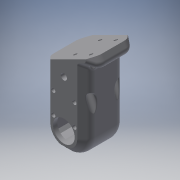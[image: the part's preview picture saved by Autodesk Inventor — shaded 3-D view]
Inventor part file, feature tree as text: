
AUTODESK INVENTOR PART (.ipt)
format: ipt  version: 2018 (Build 220112000, 112)  size: 1,027,072 bytes
history: native  units: mm
features: sketch x30, projected_geometry x26, extrude x23, hole x10, fillet x10, chamfer x3, mirror x1, plane x1
ambient origin geometry x8: Origin, YZ Plane, XZ Plane, XY Plane, X Axis, Y Axis, Z Axis, Center Point
bodies: Solid1 (feature_tree)
feature tree (104):
  extrude  "Extrusion1"  Depth=45.0mm
  extrude  "Extrusion2"  Depth=2.25mm
  hole  "Hole1"  [1 undecoded]
  hole  "Hole2"  [1 undecoded]
  fillet  "Fillet1"  Radius=14.0mm
  extrude  "Extrusion3"  Depth=18.5mm
  extrude  "Extrusion4"  Depth=10.0mm
  extrude  "Extrusion5"  Depth=2.0mm
  extrude  "Extrusion6"  Depth=2.0mm
  hole  "Hole3"  [1 undecoded]
  extrude  "Extrusion7"  Depth=0.5mm
  extrude  "Extrusion8"  Depth=5.0mm TaperAngle=0.0deg
  extrude  "Extrusion9"  Depth=10.0mm
  extrude  "Extrusion10"  Depth=10.0mm
  extrude  "Extrusion11"  Depth=14.5mm
  extrude  "Extrusion12"  Depth=20.0mm
  extrude  "Extrusion13"  Depth=5.0mm
  extrude  "Extrusion14"  Depth=2.25mm
  extrude  "Extrusion15"  Depth=5.0mm
  extrude  "Extrusion16"  Depth=9.0mm
  extrude  "Extrusion17"  Depth=1.0mm
  chamfer  "Chamfer1"  Distance=1.0mm
  fillet  "Fillet7"  Radius=20.7mm
  fillet  "Fillet8"  Radius=32.0mm
  mirror  "Mirror1"
  extrude  "Extrusion24"  Depth=1.0mm TaperAngle=0.0deg
  extrude  "Extrusion25"  Depth=8.0mm
  extrude  "Extrusion26"  Depth=0.2mm TaperAngle=0.0deg
  extrude  "Extrusion27"  Depth=0.5mm TaperAngle=0.0deg
  extrude  "Extrusion28"  Depth=5.0mm TaperAngle=0.0deg
  chamfer  "Chamfer5"  Distance=5.0mm
  fillet  "Fillet18"  Radius=0.2mm
  fillet  "Fillet19"  Radius=0.2mm
  extrude  "Extrusion29"  Depth=1.5mm
  chamfer  "Chamfer6"  Distance=40.0mm
  hole  "Hole10"  [1 undecoded]
  plane  "Work Plane2"
  hole  "Hole11"  [1 undecoded]
  fillet  "Fillet20"  Radius=10.0mm
  sketch  "Sketch43"  dims[d102=2.5mm d103=2.0mm d104=45.0deg d105=1.5mm]
  hole  "Hole12"  [1 undecoded]
  hole  "Hole13"  [1 undecoded]
  hole  "Hole14"  [1 undecoded]
  fillet  "Fillet21"  Radius=8.0mm
  fillet  "Fillet22"  Radius=10.0mm
  hole  "Hole15"  [1 undecoded]
  fillet  "Fillet23"  Radius=2.0mm
  hole  "Hole16"  [1 undecoded]
  fillet  "Fillet24"  Radius=8.0mm
  sketch  "Sketch1"  dims[d0=24.5mm d1=45.0mm]
  sketch  "Sketch2"  dims[d2=1.95mm d3=0.0mm d4=2.25mm]
  projected_geometry  "Projected Loop1"
  sketch  "Sketch3"  dims[d5=20.0mm d6=2.25mm]
  projected_geometry  "Projected Loop2"
  sketch  "Sketch4"  dims[d7=5.25mm d8=5.25mm d9=14.0mm]
  projected_geometry  "Projected Loop3"
  sketch  "Sketch5"  dims[d10=5.25mm d11=18.5mm]
  projected_geometry  "Projected Loop4"
  sketch  "Sketch6"  dims[d12=10.0mm d13=0.0mm d14=20.5mm]
  projected_geometry  "Projected Loop5"
  sketch  "Sketch7"  dims[d15=2.0mm d16=2.195mm]
  projected_geometry  "Projected Loop6"
  sketch  "Sketch8"  dims[d17=2.0mm]
  projected_geometry  "Projected Loop7"
  sketch  "Sketch9"  dims[d18=2.4mm d19=6.0mm d20=4.4mm d21=2.0mm d22=90.0deg d23=8.0mm d24=20.594885mm d25=20.5mm]
  projected_geometry  "Projected Loop8"
  projected_geometry  "Projected Loop9"
  sketch  "Sketch10"  dims[d26=26.65mm d27=2.0mm]
  projected_geometry  "Projected Loop10"
  projected_geometry  "Projected Loop11"
  sketch  "Sketch11"  dims[d28=2.0mm]
  projected_geometry  "Projected Loop12"
  sketch  "Sketch12"  dims[d29=2.4mm d30=6.0mm d31=4.4mm d32=2.0mm d33=90.0deg d34=8.0mm d35=20.594885mm d36=0.5mm]
  sketch  "Sketch13"  dims[d37=18.0mm d38=5.0mm d39=0.0mm]
  sketch  "Sketch14"  dims[d41=10.0mm d42=0.0mm d43=24.5mm]
  projected_geometry  "Projected Loop13"
  sketch  "Sketch15"  dims[d44=1.15mm d45=0.0mm d46=10.0mm]
  sketch  "Sketch16"  dims[d47=21.0mm d48=14.5mm]
  projected_geometry  "Projected Loop14"
  sketch  "Sketch17"  dims[d49=20.0mm d50=14.5mm]
  projected_geometry  "Projected Loop15"
  sketch  "Sketch18"  dims[d51=24.5mm d52=5.0mm]
  projected_geometry  "Projected Loop16"
  sketch  "Sketch19"  dims[d53=5.0mm d54=2.25mm]
  projected_geometry  "Projected Loop17"
  sketch  "Sketch20"  dims[d55=2.25mm d56=5.0mm]
  projected_geometry  "Projected Loop18"
  sketch  "Sketch35"  dims[d57=5.0mm d58=9.0mm]
  projected_geometry  "Projected Loop28"
  sketch  "Sketch36"  dims[d59=14.75mm d60=4.0mm d61=1.0mm d62=0.0mm d63=20.7mm]
  projected_geometry  "Projected Loop29"
  sketch  "Sketch37"  dims[d64=2.4mm d65=6.0mm d66=4.4mm d67=2.0mm d68=90.0deg d69=8.0mm d70=20.594885mm d72=32.0mm]
  sketch  "Sketch38"  dims[d73=5.0mm d74=0.0mm d75=1.0mm d76=0.0mm]
  sketch  "Sketch39"  dims[d77=12.25mm d78=0.0mm d80=8.0mm]
  projected_geometry  "Projected Loop30"
  sketch  "Sketch40"  dims[d81=4.5mm d82=0.0mm d84=0.2mm d85=0.0mm]
  projected_geometry  "Projected Loop31"
  sketch  "Sketch41"  dims[d86=21.0mm d87=0.5mm d88=0.0mm]
  projected_geometry  "Projected Loop32"
  projected_geometry  "Projected Loop33"
  sketch  "Sketch42"  dims[d91=8.0mm d92=0.0mm d93=5.0mm d94=0.0mm d95=5.0mm d96=0.0mm d98=0.2mm d99=0.0mm d100=0.2mm d101=0.0mm]
  projected_geometry  "Projected Loop34"
  sketch  "Sketch44"  dims[d114=0.5mm d187=40.0mm d188=70.0mm d189=20.0mm d190=10.0mm d191=0.0mm d192=10.0mm d193=0.0mm d194=2.0mm d195=0.0mm d196=2.0mm d197=0.0mm d198=8.0mm d199=10.0mm d200=2.0mm d201=0.0mm d204=7.0mm d205=2.0mm d206=45.0deg d207=5.0mm d208=8.0mm d209=15.0mm d210=2.0mm d211=0.0mm d212=1.5mm d213=2.0mm d214=45.0deg d215=24.0mm d216=17.0mm d217=3.5mm d218=3.2mm d219=6.0mm d220=9.4mm d221=2.0mm d222=90.0deg d223=8.0mm d224=20.594885mm d225=6.0mm d226=6.0mm d227=9.4mm d228=2.0mm d229=90.0deg d230=69.0mm d231=0.0mm d232=1.0mm d233=8.0mm d234=2.459mm d235=6.0mm d236=9.4mm d237=2.0mm d238=90.0deg d239=34.0mm d240=20.594885mm d241=3.2mm d242=6.0mm d243=6.3mm d244=2.0mm d245=90.0deg d246=20.55mm d247=0.0mm d248=6.0mm d249=6.0mm d250=6.3mm d251=2.0mm d252=90.0deg d253=10.0mm d254=0.0mm d255=1.5mm d256=0.75mm d257=4.0mm d258=6.0mm d259=4.4mm d260=2.0mm d261=90.0deg d262=2.5mm d263=0.0mm d264=1.0mm d265=4.0mm d266=6.0mm d267=4.4mm d268=2.0mm d269=90.0deg d270=2.5mm d271=0.0mm d272=0.5mm]
  projected_geometry  "Projected Loop35"
note: 10 required parameter values undecoded (feature->parameter linkage not recoverable at this tier; creation-order binding heuristic only, values carry confidence <= 0.55)
